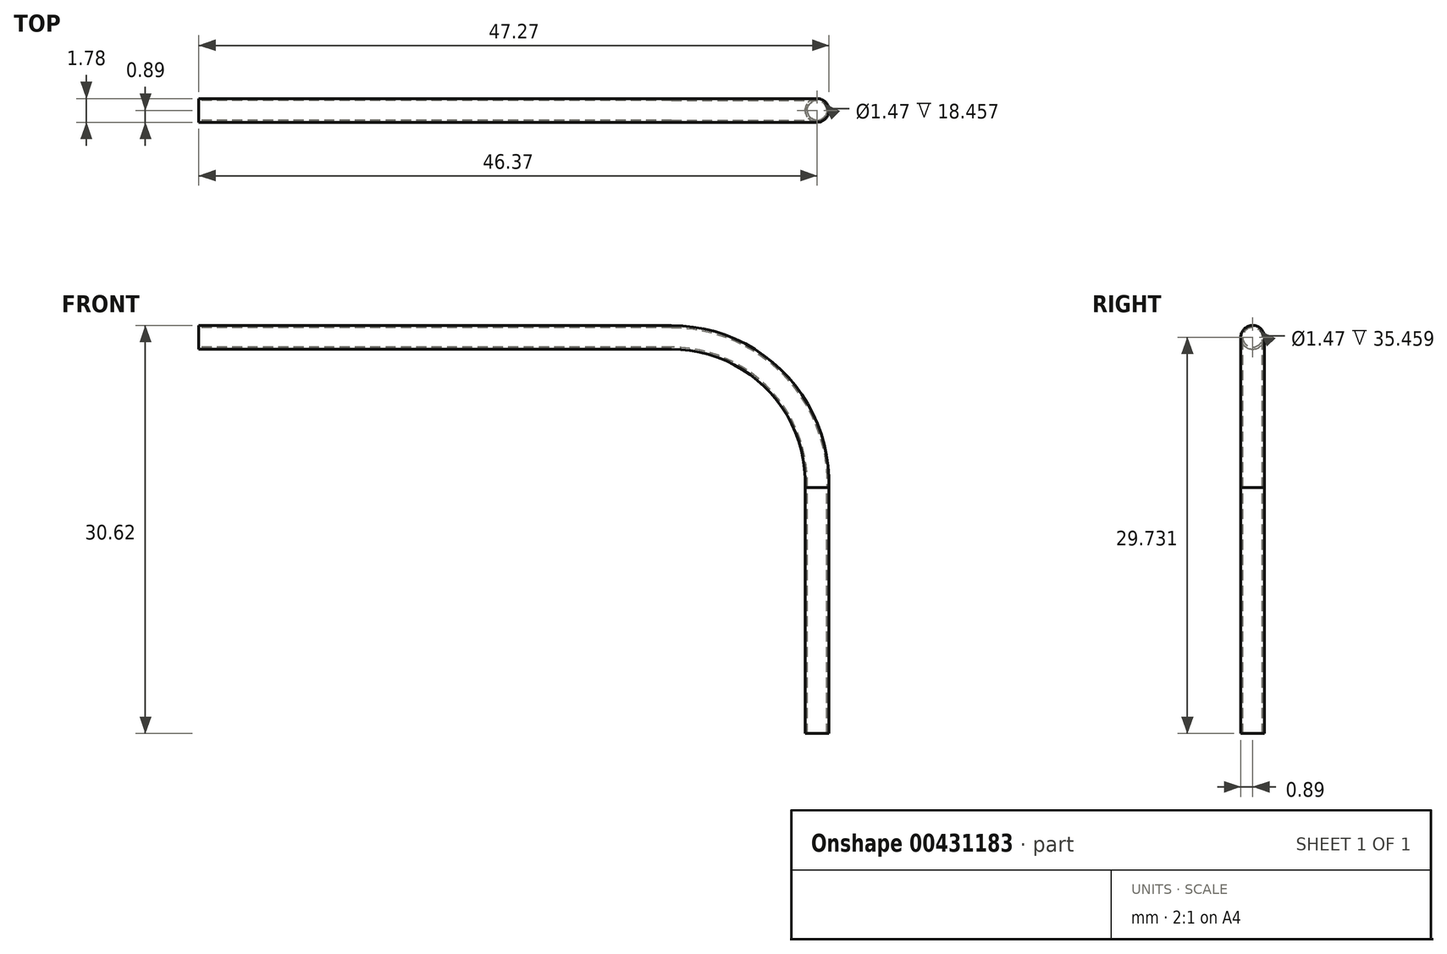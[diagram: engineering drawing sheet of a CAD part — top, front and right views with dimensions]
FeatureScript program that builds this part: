
annotation { "Feature Type Name" : "Feature", "Feature Type Description" : "" }
export const myFeature = defineFeature(function(context is Context, id is Id, definition is map)
    precondition{}
    {
        {
            var Q0;
            Q0=qCreatedBy(makeId("Front.planeOp"),FACE);
            var sketch = newSketch(context, id + "F0", { "sketchPlane" : qUnion([Q0])});
            skLineSegment(sketch, "E0", {"start": v(0, 0) * mm, "end": v(0, 18.46) * mm});
            skLineSegment(sketch, "E1", {"start": v(-10.91, 29.73) * mm, "end": v(-46.37, 29.73) * mm});
            skArc(sketch, "E2", {"start": v(-10.91, 29.73) * mm, "mid": v(-3.07, 26.4) * mm, "end": v(0, 18.46) * mm});
            skSolve(sketch);
        }
        {
            var Q0;
            Q0=qCreatedBy(makeId("Top.planeOp"),FACE);
            var sketch = newSketch(context, id + "F1", { "sketchPlane" : qUnion([Q0])});
            skCircle(sketch, "E3", {"center": v(0, 0) * mm, "radius": 0.89 * mm});
            skSolve(sketch);
        }
        {
            var Q0;
            Q0=makeQuery(id+"F1.imprint","IMPRINT",FACE,{"disambiguationData":[TD([[makeQuery(id+"F1.imprint","IMPRINT",EDGE,{"derivedFrom":sQuery(id+"F1.wireOp",EDGE,"E3")}),1.0]])]});
            var Q1;
            Q1=sQuery(id+"F0.wireOp",EDGE,"E0");
            var Q2;
            Q2=sQuery(id+"F0.wireOp",EDGE,"E2");
            var Q3;
            Q3=sQuery(id+"F0.wireOp",EDGE,"E1");
            sweep(context, id + "F2", {"profiles" : qUnion([Q0]), "path" : qUnion([Q1, Q2, Q3])});
        }
        {
            var Q0;
            Q0=qCreatedBy(makeId("Top.planeOp"),FACE);
            var sketch = newSketch(context, id + "F3", { "sketchPlane" : qUnion([Q0])});
            skCircle(sketch, "E4", {"center": v(0, 0) * mm, "radius": 0.74 * mm});
            skSolve(sketch);
        }
        {
            var Q0;
            Q0=makeQuery(id+"F3.imprint","IMPRINT",FACE,{"disambiguationData":[TD([[makeQuery(id+"F3.imprint","IMPRINT",EDGE,{"derivedFrom":sQuery(id+"F3.wireOp",EDGE,"E4")}),1.0]])]});
            var Q1;
            Q1=sQuery(id+"F0.wireOp",EDGE,"E0");
            var Q2;
            Q2=sQuery(id+"F0.wireOp",EDGE,"E2");
            var Q3;
            Q3=sQuery(id+"F0.wireOp",EDGE,"E1");
            sweep(context, id + "F4", {"operationType" : NewBodyOperationType.REMOVE, "profiles" : qUnion([Q0]), "path" : qUnion([Q1, Q2, Q3])});
        }
    });
